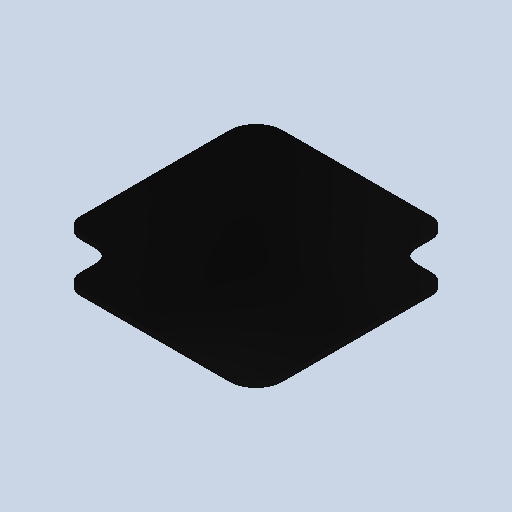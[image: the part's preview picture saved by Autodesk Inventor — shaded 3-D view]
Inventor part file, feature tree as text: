
AUTODESK INVENTOR PART (.ipt)
format: ipt  version: 2022.3 (Build 263350000, 350)  size: 68,608 bytes
history: native  units: mm (DEFAULTED — no unit token found)
features: fillet x1
ambient origin geometry x8: Origin, YZ Plane, XZ Plane, XY Plane, X Axis, Y Axis, Z Axis, Center Point
bodies: Solid1 (feature_tree)
feature tree (1):
  fillet  "Fillet3"  [1 undecoded]
note: 1 required parameter value undecoded (feature->parameter linkage not recoverable at this tier; creation-order binding heuristic only, values carry confidence <= 0.55)
